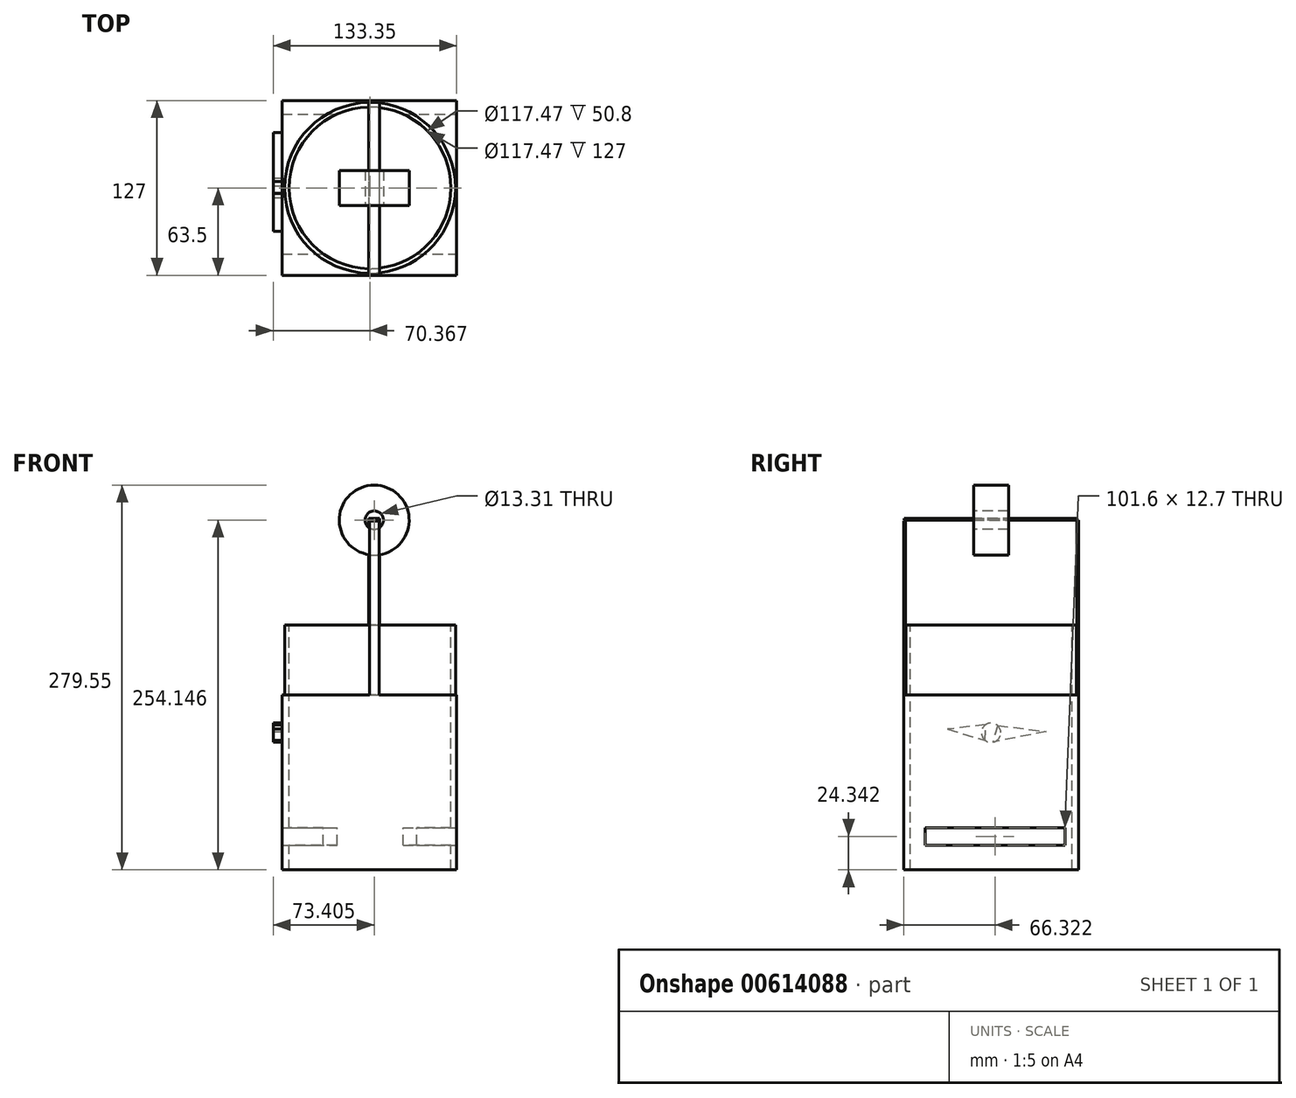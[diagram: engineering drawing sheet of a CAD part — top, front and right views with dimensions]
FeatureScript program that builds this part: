
annotation { "Feature Type Name" : "Feature", "Feature Type Description" : "" }
export const myFeature = defineFeature(function(context is Context, id is Id, definition is map)
    precondition{}
    {
        {
            var Q0;
            Q0=qCreatedBy(makeId("Front.planeOp"),FACE);
            var sketch = newSketch(context, id + "F0", { "sketchPlane" : qUnion([Q0])});
            skLineSegment(sketch, "E0", {"start": v(66.7, 0) * mm, "end": v(66.7, 127) * mm});
            skLineSegment(sketch, "E1", {"start": v(66.7, 127) * mm, "end": v(193.7, 127) * mm});
            skLineSegment(sketch, "E2", {"start": v(193.7, 127) * mm, "end": v(193.7, 0) * mm});
            skLineSegment(sketch, "E3", {"start": v(193.7, 0) * mm, "end": v(66.7, 0) * mm});
            skSolve(sketch);
        }
        {
            var Q0;
            Q0=makeQuery(id+"F0.imprint","IMPRINT",FACE,{"disambiguationData":[TD([[makeQuery(id+"F0.imprint","IMPRINT",EDGE,{"derivedFrom":sQuery(id+"F0.wireOp",EDGE,"E0")}),-1.0]])]});
            extrude(context, id + "F1", {"entities" : qUnion([Q0]), "depth" : 127 * mm, "offsetDistance" : 25.4 * mm});
        }
        {
            var Q0;
            Q0=makeQuery(id+"F1.opExtrude","SWEPT_FACE",FACE,{"disambiguationData":[OSD([sQuery(id+"F0.wireOp",EDGE,"E1")])]});
            var sketch = newSketch(context, id + "F2", { "sketchPlane" : qUnion([Q0])});
            skCircle(sketch, "E4", {"center": v(130.72, -63.5) * mm, "radius": 62.05 * mm});
            skSolve(sketch);
        }
        {
            var Q0;
            Q0=makeQuery(id+"F2.imprint","IMPRINT",FACE,{"disambiguationData":[TD([[makeQuery(id+"F2.imprint","IMPRINT",EDGE,{"derivedFrom":sQuery(id+"F2.wireOp",EDGE,"E4")}),1.0]])]});
            extrude(context, id + "F3", {"entities" : qUnion([Q0]), "depth" : 50.8 * mm, "offsetDistance" : 25.4 * mm});
        }
        {
            var Q0;
            Q0=makeQuery(id+"F1.opExtrude","SWEPT_FACE",FACE,{"disambiguationData":[OSD([sQuery(id+"F0.wireOp",EDGE,"E2")])]});
            var sketch = newSketch(context, id + "F4", { "sketchPlane" : qUnion([Q0])});
            skLineSegment(sketch, "E5", {"start": v(-111.48, 18) * mm, "end": v(-111.48, 30.7) * mm});
            skLineSegment(sketch, "E6", {"start": v(-111.48, 30.7) * mm, "end": v(-9.88, 30.7) * mm});
            skLineSegment(sketch, "E7", {"start": v(-9.88, 30.7) * mm, "end": v(-9.88, 18) * mm});
            skLineSegment(sketch, "E8", {"start": v(-9.88, 18) * mm, "end": v(-111.48, 18) * mm});
            skSolve(sketch);
        }
        {
            var Q0;
            Q0=makeQuery(id+"F4.imprint","IMPRINT",FACE,{"disambiguationData":[TD([[makeQuery(id+"F4.imprint","IMPRINT",EDGE,{"derivedFrom":sQuery(id+"F4.wireOp",EDGE,"E5")}),-1.0]])]});
            extrude(context, id + "F5", {"entities" : qUnion([Q0]), "operationType" : NewBodyOperationType.REMOVE, "oppositeDirection" : true, "depth" : 127 * mm, "offsetDistance" : 25.4 * mm});
        }
        {
            var Q0;
            Q0=makeQuery(id+"F1.opExtrude","CAP_FACE",FACE,{"disambiguationData":[OSD([sQuery(id+"F0.wireOp",EDGE,"E0"),sQuery(id+"F0.wireOp",EDGE,"E1"),sQuery(id+"F0.wireOp",EDGE,"E2"),sQuery(id+"F0.wireOp",EDGE,"E3")])],"isStart":true});
            var sketch = newSketch(context, id + "F6", { "sketchPlane" : qUnion([Q0])});
            skLineSegment(sketch, "E9", {"start": v(-137.68, 127) * mm, "end": v(-137.68, 254) * mm});
            skLineSegment(sketch, "E10", {"start": v(-137.68, 254) * mm, "end": v(-129.72, 254) * mm});
            skLineSegment(sketch, "E11", {"start": v(-129.72, 254) * mm, "end": v(-129.72, 127) * mm});
            skLineSegment(sketch, "E12", {"start": v(-129.72, 127) * mm, "end": v(-137.68, 127) * mm});
            skSolve(sketch);
        }
        {
            var Q0;
            Q0=qCreatedBy(makeId("Front.planeOp"),FACE);
            cPlane(context, id + "F7", {"entities" : qUnion([Q0]), "cplaneType" : CPlaneType.OFFSET, "offset" : 63.5 * mm, "width" : 152.4 * mm, "height" : 152.4 * mm});
        }
        {
            var Q0;
            Q0=makeQuery(id+"F6.imprint","IMPRINT",FACE,{"disambiguationData":[TD([[makeQuery(id+"F6.imprint","IMPRINT",EDGE,{"derivedFrom":sQuery(id+"F6.wireOp",EDGE,"E9")}),-1.0]])]});
            extrude(context, id + "F8", {"entities" : qUnion([Q0]), "oppositeDirection" : true, "depth" : 1.27 * mm, "offsetDistance" : 25.4 * mm});
        }
        {
            var Q0;
            Q0=makeQuery(id+"F1.opExtrude","CAP_FACE",FACE,{"disambiguationData":[OSD([sQuery(id+"F0.wireOp",EDGE,"E0"),sQuery(id+"F0.wireOp",EDGE,"E1"),sQuery(id+"F0.wireOp",EDGE,"E2"),sQuery(id+"F0.wireOp",EDGE,"E3")])],"isStart":false});
            var sketch = newSketch(context, id + "F9", { "sketchPlane" : qUnion([Q0])});
            skLineSegment(sketch, "E13", {"start": v(130.2, 127) * mm, "end": v(130.2, 253.46) * mm});
            skLineSegment(sketch, "E14", {"start": v(130.2, 253.46) * mm, "end": v(137.3, 253.46) * mm});
            skLineSegment(sketch, "E15", {"start": v(137.3, 253.46) * mm, "end": v(137.3, 127) * mm});
            skLineSegment(sketch, "E16", {"start": v(137.3, 127) * mm, "end": v(130.2, 127) * mm});
            skSolve(sketch);
        }
        {
            var Q0;
            Q0=makeQuery(id+"F9.imprint","IMPRINT",FACE,{"disambiguationData":[TD([[makeQuery(id+"F9.imprint","IMPRINT",EDGE,{"derivedFrom":sQuery(id+"F9.wireOp",EDGE,"E13")}),-1.0]])]});
            extrude(context, id + "F10", {"entities" : qUnion([Q0]), "operationType" : NewBodyOperationType.ADD, "oppositeDirection" : true, "depth" : 1.27 * mm, "offsetDistance" : 25.4 * mm});
        }
        {
            var Q0;
            Q0=makeQuery(id+"F8.opExtrude","SWEPT_FACE",FACE,{"disambiguationData":[OSD([sQuery(id+"F6.wireOp",EDGE,"E10")])]});
            var sketch = newSketch(context, id + "F11", { "sketchPlane" : qUnion([Q0])});
            skLineSegment(sketch, "E17", {"start": v(129.72, -1.27) * mm, "end": v(129.72, -126.75) * mm});
            skLineSegment(sketch, "E18", {"start": v(129.72, -126.75) * mm, "end": v(137.68, -126.75) * mm});
            skLineSegment(sketch, "E19", {"start": v(137.68, -126.75) * mm, "end": v(137.68, 0) * mm});
            skLineSegment(sketch, "E20", {"start": v(137.68, 0) * mm, "end": v(129.72, 0) * mm});
            skSolve(sketch);
        }
        {
            var Q0;
            Q0=makeQuery(id+"F11.imprint","IMPRINT",FACE,{"disambiguationData":[TD([[makeQuery(id+"F11.imprint","IMPRINT",EDGE,{"derivedFrom":sQuery(id+"F11.wireOp",EDGE,"E17")}),1.0]])]});
            extrude(context, id + "F12", {"entities" : qUnion([Q0]), "depth" : 1.27 * mm, "offsetDistance" : 25.4 * mm});
        }
        {
            var Q0;
            Q0=qCreatedBy(id+"F7.planeOp",FACE);
            var sketch = newSketch(context, id + "F13", { "sketchPlane" : qUnion([Q0])});
            skCircle(sketch, "E21", {"center": v(133.75, 254.15) * mm, "radius": 25.4 * mm});
            skCircle(sketch, "E22", {"center": v(133.75, 254.15) * mm, "radius": 6.65 * mm});
            skSolve(sketch);
        }
        {
            var Q0;
            Q0=makeQuery(id+"F13.imprint","IMPRINT",FACE,{"disambiguationData":[TD([[makeQuery(id+"F13.imprint","IMPRINT",EDGE,{"derivedFrom":sQuery(id+"F13.wireOp",EDGE,"E21")}),1.0]])]});
            extrude(context, id + "F14", {"entities" : qUnion([Q0]), "endBound" : BoundingType.SYMMETRIC, "oppositeDirection" : true, "depth" : 25.4 * mm, "offsetDistance" : 25.4 * mm});
        }
        {
            var Q0;
            Q0=makeQuery(id+"F3.opExtrude","CAP_FACE",FACE,{"disambiguationData":[OSD([sQuery(id+"F2.wireOp",EDGE,"E4")])],"isStart":false});
            var sketch = newSketch(context, id + "F15", { "sketchPlane" : qUnion([Q0])});
            skCircle(sketch, "E23", {"center": v(130.72, -63.5) * mm, "radius": 58.73 * mm});
            skSolve(sketch);
        }
        {
            var Q0;
            Q0=makeQuery(id+"F15.imprint","IMPRINT",FACE,{"disambiguationData":[TD([[makeQuery(id+"F15.imprint","IMPRINT",EDGE,{"derivedFrom":sQuery(id+"F15.wireOp",EDGE,"E23")}),1.0]])]});
            extrude(context, id + "F16", {"entities" : qUnion([Q0]), "operationType" : NewBodyOperationType.REMOVE, "oppositeDirection" : true, "depth" : 177.8 * mm, "offsetDistance" : 25.4 * mm});
        }
        {
            var Q0;
            Q0=makeQuery(id+"F1.opExtrude","SWEPT_FACE",FACE,{"disambiguationData":[OSD([sQuery(id+"F0.wireOp",EDGE,"E1")])]});
            var sketch = newSketch(context, id + "F17", { "sketchPlane" : qUnion([Q0])});
            skCircle(sketch, "E24", {"center": v(129.7, -63.5) * mm, "radius": 55.77 * mm});
            skPoint(sketch, "E24.centerSnap0", {"position": v(193.7, -63.5) * mm});
            skSolve(sketch);
        }
        {
            var Q0;
            Q0=makeQuery(id+"F17.imprint","IMPRINT",FACE,{"disambiguationData":[TD([[makeQuery(id+"F17.imprint","IMPRINT",EDGE,{"derivedFrom":sQuery(id+"F17.wireOp",EDGE,"E24")}),1.0]])]});
            extrude(context, id + "F18", {"entities" : qUnion([Q0]), "operationType" : NewBodyOperationType.REMOVE, "endBound" : BoundingType.THROUGH_ALL, "oppositeDirection" : true, "depth" : 76.2 * mm, "offsetDistance" : 25.4 * mm});
        }
        {
            var Q0;
            Q0=makeQuery(id+"F1.opExtrude","SWEPT_FACE",FACE,{"disambiguationData":[OSD([sQuery(id+"F0.wireOp",EDGE,"E0")])]});
            var sketch = newSketch(context, id + "F19", { "sketchPlane" : qUnion([Q0])});
            skCircle(sketch, "E25", {"center": v(63.5, 99.75) * mm, "radius": 7.02 * mm});
            skPoint(sketch, "E25.centerSnap0", {"position": v(63.5, 127) * mm});
            skLineSegment(sketch, "E26", {"start": v(58.64, 104.82) * mm, "end": v(16.57, 99.75) * mm});
            skLineSegment(sketch, "E27", {"start": v(16.57, 99.75) * mm, "end": v(59.68, 93.23) * mm});
            skLineSegment(sketch, "E28", {"start": v(68.15, 105.02) * mm, "end": v(109.55, 99.75) * mm});
            skLineSegment(sketch, "E29", {"start": v(109.55, 99.75) * mm, "end": v(65.8, 93.12) * mm});
            skSolve(sketch);
        }
        {
            var Q0;
            {var subQ0=sQuery(id+"F19.wireOp",EDGE,"E25");var subQ1=makeQuery(id+"F19.imprint","IMPRINT",VERTEX,{"derivedFrom":subQ0});Q0=makeQuery(id+"F19.imprint","IMPRINT",FACE,{"disambiguationData":[TD([[makeQuery(id+"F19.imprint","IMPRINT",EDGE,{"disambiguationData":[TD([[subQ1,1.0]])],"derivedFrom":subQ0}),1.0]])]});}
            extrude(context, id + "F20", {"entities" : qUnion([Q0]), "depth" : 6.35 * mm, "offsetDistance" : 25.4 * mm});
        }
        {
            var Q0;
            Q0=makeQuery(id+"F1.opExtrude","SWEPT_FACE",FACE,{"disambiguationData":[OSD([sQuery(id+"F0.wireOp",EDGE,"E0")])]});
            var sketch = newSketch(context, id + "F21", { "sketchPlane" : qUnion([Q0])});
            skLineSegment(sketch, "E30", {"start": v(58.85, 105.02) * mm, "end": v(23.46, 100.59) * mm});
            skLineSegment(sketch, "E31", {"start": v(23.46, 100.59) * mm, "end": v(62.13, 92.87) * mm});
            skLineSegment(sketch, "E32", {"start": v(67.1, 105.78) * mm, "end": v(97.94, 98.2) * mm});
            skLineSegment(sketch, "E33", {"start": v(97.94, 98.2) * mm, "end": v(64.62, 92.82) * mm});
            skArc(sketch, "E34", {"start": v(58.85, 105.02) * mm, "mid": v(62.97, 105.46) * mm, "end": v(67.1, 105.78) * mm});
            skLineSegment(sketch, "E35", {"start": v(58.85, 105.02) * mm, "end": v(62.13, 92.87) * mm});
            skLineSegment(sketch, "E36", {"start": v(67.1, 105.78) * mm, "end": v(64.62, 92.82) * mm});
            skSolve(sketch);
        }
        {
            var Q0;
            {var subQ0=sQuery(id+"F21.wireOp",EDGE,"E30");Q0=makeQuery(id+"F21.imprint","IMPRINT",FACE,{"disambiguationData":[TD([[makeQuery(id+"F21.imprint","IMPRINT",EDGE,{"derivedFrom":subQ0}),1.0]])]});}
            extrude(context, id + "F22", {"entities" : qUnion([Q0]), "depth" : 6.35 * mm, "offsetDistance" : 25.4 * mm});
        }
        {
            var Q0;
            Q0=makeQuery(id+"F1.opExtrude","SWEPT_FACE",FACE,{"disambiguationData":[OSD([sQuery(id+"F0.wireOp",EDGE,"E0")])]});
            var sketch = newSketch(context, id + "F23", { "sketchPlane" : qUnion([Q0])});
            skLineSegment(sketch, "E37", {"start": v(67.54, 105.5) * mm, "end": v(95.15, 102.23) * mm});
            skLineSegment(sketch, "E38", {"start": v(67.98, 93.8) * mm, "end": v(67.54, 105.5) * mm});
            skLineSegment(sketch, "E39", {"start": v(95.15, 102.23) * mm, "end": v(67.21, 93.8) * mm});
            skSolve(sketch);
        }
        {
            var Q0;
            {var subQ0=sQuery(id+"F23.wireOp",EDGE,"E37");Q0=makeQuery(id+"F23.imprint","IMPRINT",FACE,{"disambiguationData":[TD([[makeQuery(id+"F23.imprint","IMPRINT",EDGE,{"derivedFrom":subQ0}),-1.0]])]});}
            extrude(context, id + "F24", {"entities" : qUnion([Q0]), "depth" : 6.35 * mm, "offsetDistance" : 25.4 * mm});
        }
    });
